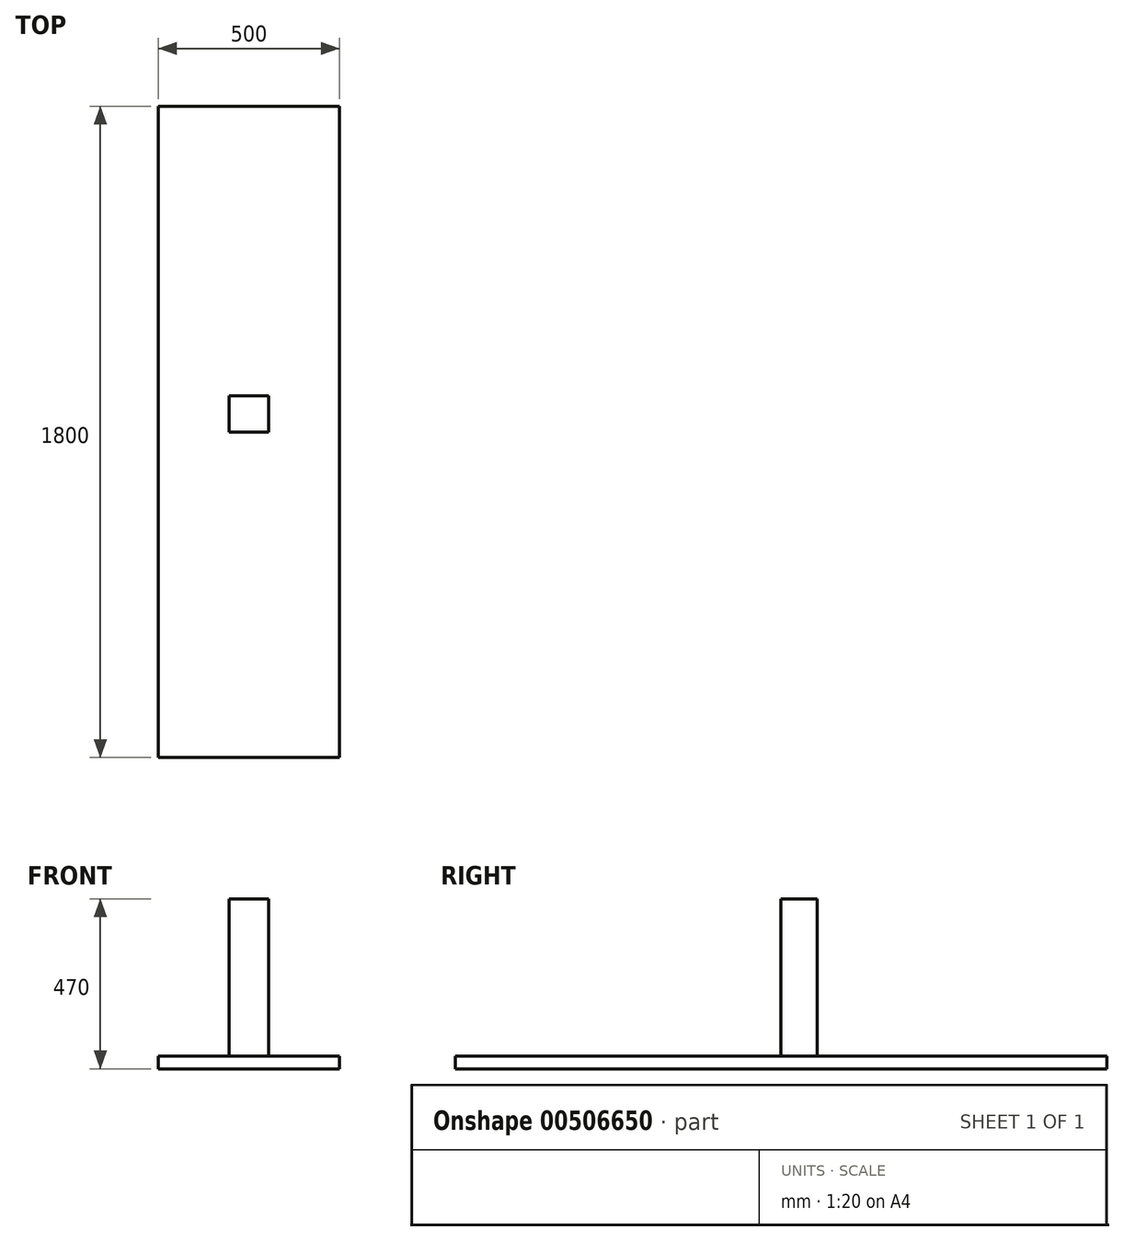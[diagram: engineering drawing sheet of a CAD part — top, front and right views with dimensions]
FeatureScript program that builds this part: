
annotation { "Feature Type Name" : "Feature", "Feature Type Description" : "" }
export const myFeature = defineFeature(function(context is Context, id is Id, definition is map)
    precondition{}
    {
        {
            var Q0;
            Q0=qCreatedBy(makeId("Front.planeOp"),FACE);
            var sketch = newSketch(context, id + "F0", { "sketchPlane" : qUnion([Q0])});
            skLineSegment(sketch, "E0.bottom", {"start": v(0, 0) * mm, "end": v(-108.58, 0) * mm});
            skLineSegment(sketch, "E0.top", {"start": v(0, 470) * mm, "end": v(-108.58, 470) * mm});
            skLineSegment(sketch, "E0.left", {"start": v(0, 0) * mm, "end": v(0, 470) * mm});
            skLineSegment(sketch, "E0.right", {"start": v(-108.58, 0) * mm, "end": v(-108.58, 470) * mm});
            skSolve(sketch);
        }
        {
            var Q0;
            Q0 = qSketchRegion(id + "F0", true);
            extrude(context, id + "F1", {"entities" : qUnion([Q0]), "depth" : 100 * mm});
        }
        {
            var Q0;
            Q0=makeQuery(id+"F1.opExtrude","CAP_FACE",FACE,{"disambiguationData":[OSD([sQuery(id+"F0.wireOp",EDGE,"E0.bottom"),sQuery(id+"F0.wireOp",EDGE,"E0.top"),sQuery(id+"F0.wireOp",EDGE,"E0.left"),sQuery(id+"F0.wireOp",EDGE,"E0.right")])],"isStart":false});
            var sketch = newSketch(context, id + "F2", { "sketchPlane" : qUnion([Q0])});
            skLineSegment(sketch, "E1", {"start": v(-54.29, 0) * mm, "end": v(-54.29, -51.2) * mm, "construction": true});
            skLineSegment(sketch, "E2", {"start": v(-54.29, 0) * mm, "end": v(-304.29, 0) * mm});
            skLineSegment(sketch, "E3", {"start": v(-304.29, 0) * mm, "end": v(-304.29, 34.63) * mm});
            skLineSegment(sketch, "E4", {"start": v(-304.29, 34.63) * mm, "end": v(-54.29, 34.63) * mm});
            skLineSegment(sketch, "E5.MirrorCS", {"start": v(-54.29, 0) * mm, "end": v(195.71, 0) * mm});
            skLineSegment(sketch, "E6.MirrorCS", {"start": v(195.71, 0) * mm, "end": v(195.71, 34.63) * mm});
            skLineSegment(sketch, "E7.MirrorCS", {"start": v(195.71, 34.63) * mm, "end": v(-54.29, 34.63) * mm});
            skSolve(sketch);
        }
        {
            var Q0;
            Q0 = qSketchRegion(id + "F2", true);
            extrude(context, id + "F3", {"entities" : qUnion([Q0]), "operationType" : NewBodyOperationType.ADD, "depth" : 1800 * mm, "symmetric" : true});
        }
    });
